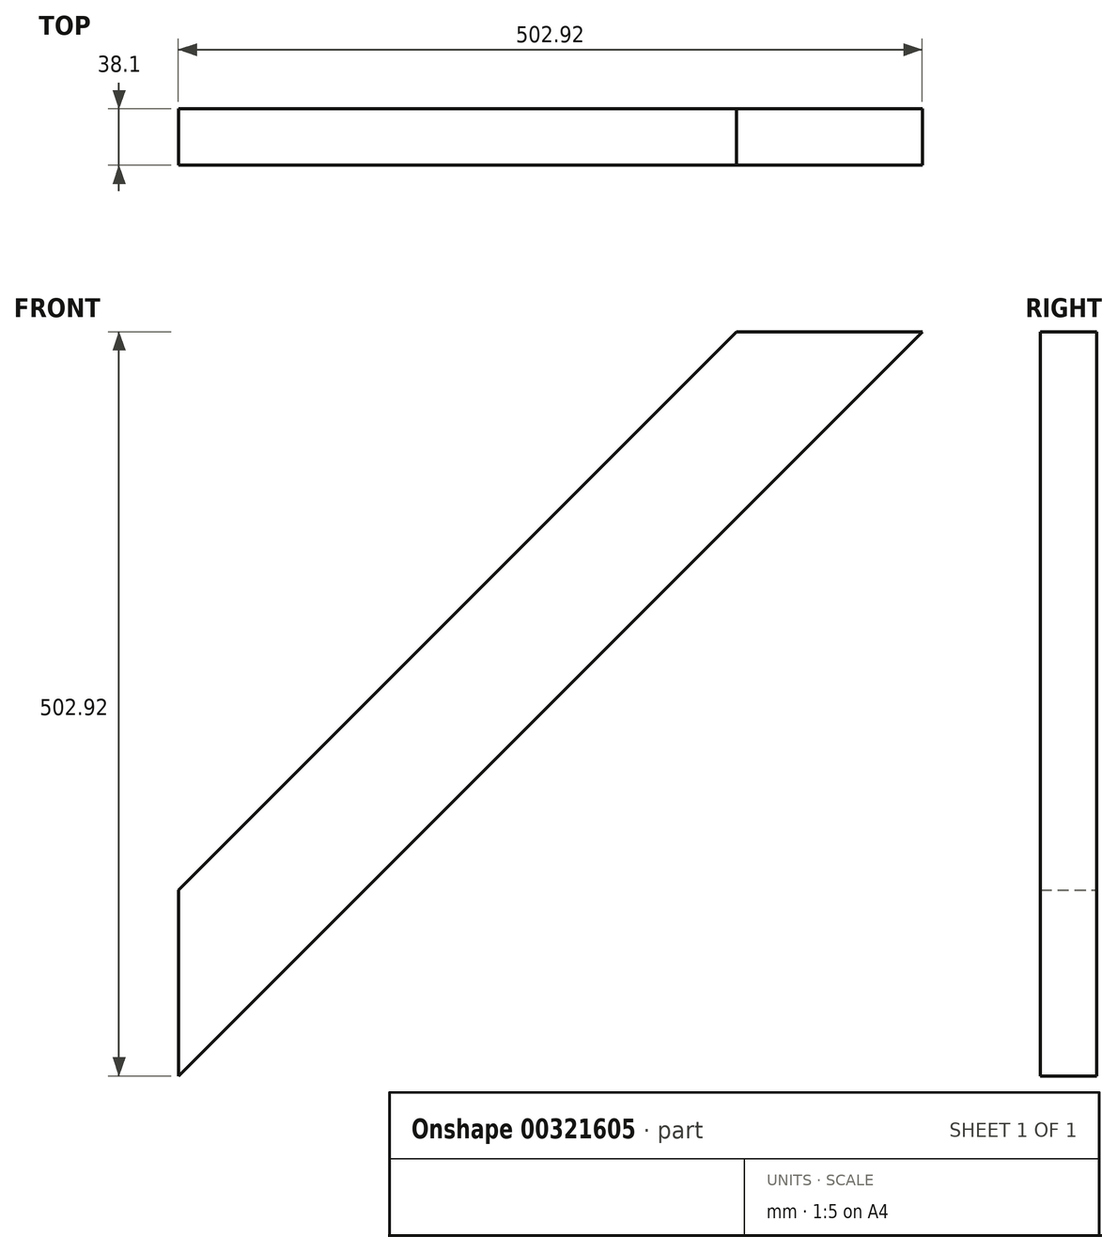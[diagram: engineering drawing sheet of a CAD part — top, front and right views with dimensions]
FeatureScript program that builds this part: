
annotation { "Feature Type Name" : "Feature", "Feature Type Description" : "" }
export const myFeature = defineFeature(function(context is Context, id is Id, definition is map)
    precondition{}
    {
        {
            var Q0;
            Q0=qCreatedBy(makeId("Front.planeOp"),FACE);
            var sketch = newSketch(context, id + "F0", { "sketchPlane" : qUnion([Q0])});
            skLineSegment(sketch, "E0", {"start": v(179.88, 303.39) * mm, "end": v(305.61, 303.39) * mm});
            skLineSegment(sketch, "E1", {"start": v(305.61, 303.39) * mm, "end": v(-197.3, -199.53) * mm});
            skLineSegment(sketch, "E2", {"start": v(-197.3, -199.53) * mm, "end": v(-197.3, -73.8) * mm});
            skLineSegment(sketch, "E3", {"start": v(-197.3, -73.8) * mm, "end": v(179.88, 303.39) * mm});
            skSolve(sketch);
        }
        {
            var Q0;
            Q0=makeQuery(id+"F0.imprint","IMPRINT",FACE,{"disambiguationData":[TD([[makeQuery(id+"F0.imprint","IMPRINT",EDGE,{"derivedFrom":sQuery(id+"F0.wireOp",EDGE,"E0")}),-1.0]])]});
            extrude(context, id + "F1", {"entities" : qUnion([Q0]), "depth" : 38.1 * mm});
        }
    });
